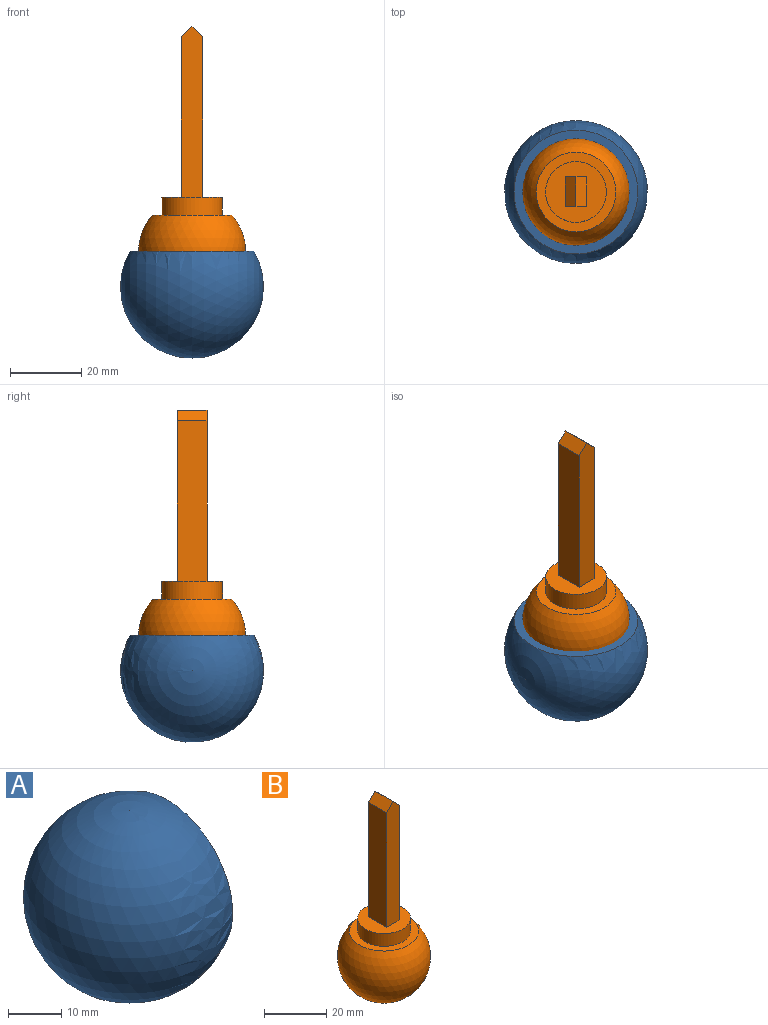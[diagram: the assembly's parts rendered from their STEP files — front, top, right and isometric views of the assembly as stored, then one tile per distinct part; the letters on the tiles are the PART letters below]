
ASSEMBLY  parts=2 mates=1
PART A: 3 faces, bbox 40x40x40 mm
  f0: plane 34.64x34.64mm, normal (1,0,0), area 294.5mm2, adj f1,f2
  f1: sphere r=20mm, area 3769.9mm2, adj f0
  f2: sphere r=17.5mm, area 3023.8mm2, adj f0
PART B: 10 faces, bbox 29.9x29.9x77.9 mm
  f0: plane 17.01x17.01mm, normal (0,0,1), area 178.1mm2, adj f3,f4,f5,f6,f7
  f1: plane 22.27x22.27mm, normal (0,0,1), area 162.1mm2, adj f2,f3
  f2: sphere r=14.96mm, area 2347.4mm2, adj f1
  f3: cylinder r=8.51mm len=17.01mm, axis (0,0,-1), area 267.2mm2, adj f0,f1
  f4: plane 45x8.33mm, normal (1,0,0), area 374.8mm2, adj f0,f5,f7,f9
  f5: plane 47.95x5.91mm, normal (0,1,0), area 274.6mm2, adj f0,f4,f6,f8,f9
  f6: plane 45x8.33mm, normal (-1,0,0), area 374.8mm2, adj f0,f5,f7,f8
  f7: plane 47.95x5.91mm, normal (0,-1,0), area 274.6mm2, adj f0,f4,f6,f8,f9
  f8: plane 8.33x2.95mm, normal (-0.71,0,0.71), area 34.8mm2, adj f5,f6,f7,f9
  f9: plane 8.33x2.95mm, normal (0.71,0,0.71), area 34.8mm2, adj f4,f5,f7,f8
PLACE A rot(axis=(0.71,0,0.71),180deg) t=(-36.62,-14.52,7.09)mm fixed
PLACE B t=(-38.13,-14.52,17.09)mm
MATE ball A.f0 <-> B.f3  axis (0,0,1) through (-38.13,-14.52,17.09)mm
